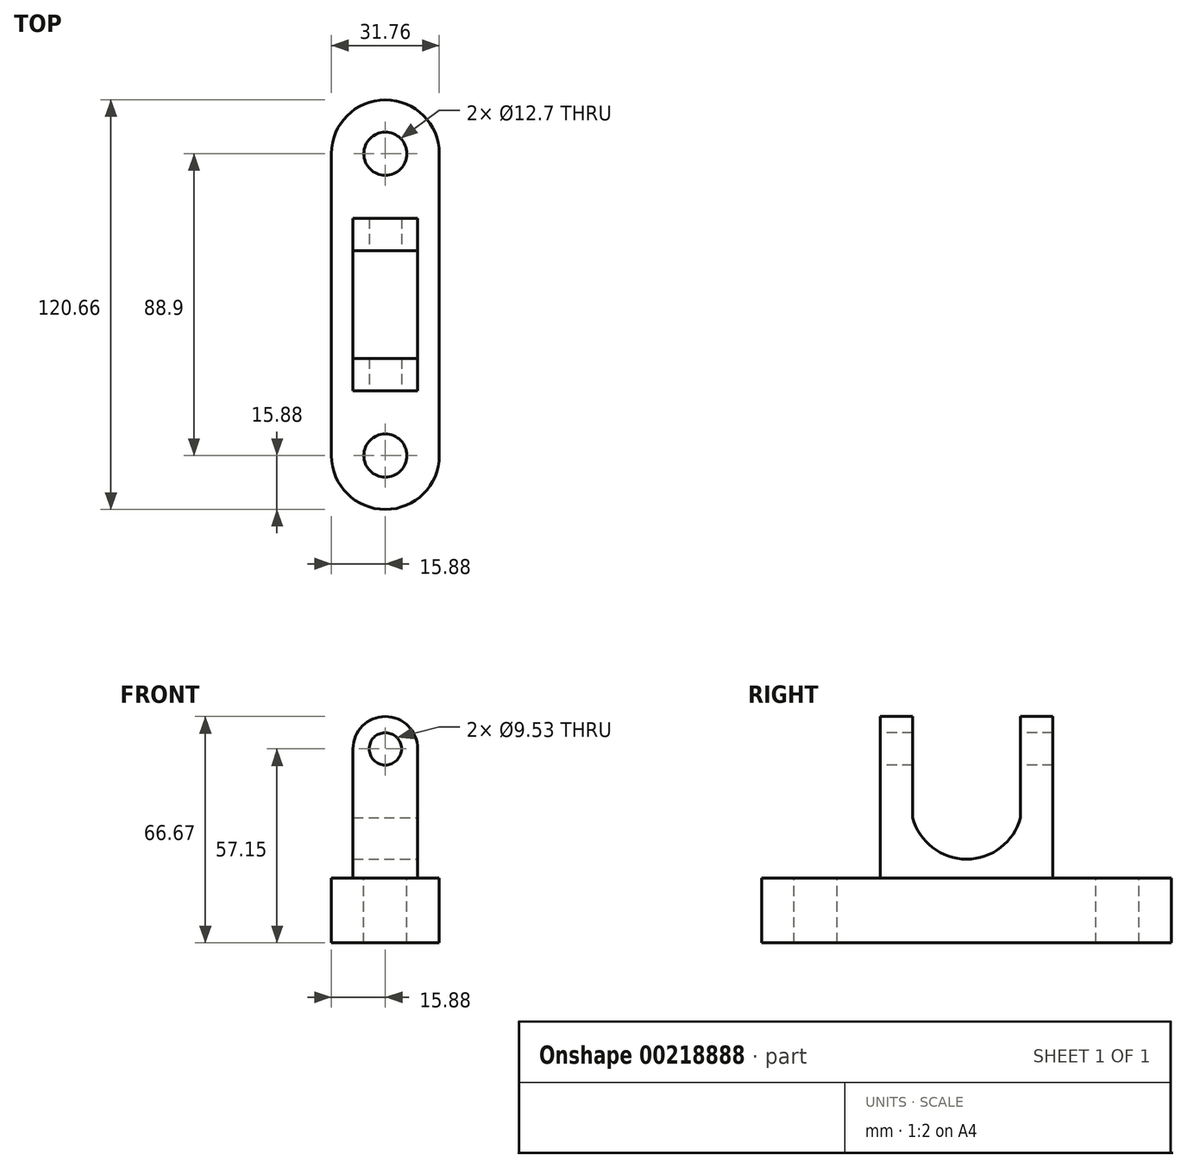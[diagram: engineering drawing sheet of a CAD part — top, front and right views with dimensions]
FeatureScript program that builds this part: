
annotation { "Feature Type Name" : "Feature", "Feature Type Description" : "" }
export const myFeature = defineFeature(function(context is Context, id is Id, definition is map)
    precondition{}
    {
        {
            var Q0;
            Q0=qCreatedBy(makeId("Top.planeOp"),FACE);
            var sketch = newSketch(context, id + "F0", { "sketchPlane" : qUnion([Q0])});
            skLineSegment(sketch, "E0.bottom", {"start": v(15.88, 44.45) * mm, "end": v(-15.88, 44.45) * mm});
            skLineSegment(sketch, "E0.top", {"start": v(15.87, -44.45) * mm, "end": v(-15.87, -44.45) * mm});
            skLineSegment(sketch, "E0.left", {"start": v(15.88, 44.45) * mm, "end": v(15.88, -44.45) * mm});
            skLineSegment(sketch, "E0.right", {"start": v(-15.87, 44.45) * mm, "end": v(-15.88, -44.45) * mm});
            skPoint(sketch, "E0.middle", {"position": v(0, 0) * mm});
            skCircle(sketch, "E1", {"center": v(0, 44.45) * mm, "radius": 15.88 * mm});
            skPoint(sketch, "E1.third.point", {"position": v(0, 60.33) * mm});
            skPoint(sketch, "E1.third.point.positionSnap0", {"position": v(0, 44.45) * mm});
            skCircle(sketch, "E2", {"center": v(0, -44.45) * mm, "radius": 15.88 * mm});
            skPoint(sketch, "E2.third.point", {"position": v(0, -60.32) * mm});
            skPoint(sketch, "E2.third.point.positionSnap0", {"position": v(0, -44.45) * mm});
            skSolve(sketch);
        }
        {
            var Q0;
            Q0 = qSketchRegion(id + "F0", true);
            extrude(context, id + "F1", {"entities" : qUnion([Q0]), "depth" : 19.05 * mm});
        }
        {
            var Q0;
            Q0=makeQuery(id+"F1.opExtrude","CAP_FACE",FACE,{"disambiguationData":[OSD([sQuery(id+"F0.wireOp",EDGE,"E0.left"),sQuery(id+"F0.wireOp",EDGE,"E0.right"),sQuery(id+"F0.wireOp",EDGE,"E1"),sQuery(id+"F0.wireOp",EDGE,"E2")])],"isStart":false});
            var sketch = newSketch(context, id + "F2", { "sketchPlane" : qUnion([Q0])});
            skCircle(sketch, "E3", {"center": v(0, -44.45) * mm, "radius": 6.35 * mm});
            skCircle(sketch, "E4", {"center": v(0, 44.45) * mm, "radius": 6.35 * mm});
            skSolve(sketch);
        }
        {
            var Q0;
            Q0 = qSketchRegion(id + "F2", true);
            extrude(context, id + "F3", {"entities" : qUnion([Q0]), "operationType" : NewBodyOperationType.REMOVE, "oppositeDirection" : true, "depth" : 25.4 * mm});
        }
        {
            var Q0;
            Q0=qCreatedBy(makeId("Front.planeOp"),FACE);
            var sketch = newSketch(context, id + "F4", { "sketchPlane" : qUnion([Q0])});
            skLineSegment(sketch, "E5.0", {"start": v(-15.88, 19.05) * mm, "end": v(15.88, 19.05) * mm});
            skLineSegment(sketch, "E6", {"start": v(-9.53, 19.05) * mm, "end": v(-9.53, 57.15) * mm});
            skLineSegment(sketch, "E7", {"start": v(-9.53, 57.15) * mm, "end": v(9.52, 57.15) * mm});
            skLineSegment(sketch, "E8", {"start": v(9.52, 57.15) * mm, "end": v(9.53, 19.05) * mm});
            skCircle(sketch, "E9", {"center": v(0, 57.15) * mm, "radius": 9.53 * mm});
            skPoint(sketch, "E9.third.point", {"position": v(0, 66.68) * mm});
            skPoint(sketch, "E9.third.point.positionSnap0", {"position": v(0, 57.15) * mm});
            skSolve(sketch);
        }
        {
            var Q0;
            Q0 = qSketchRegion(id + "F4", true);
            extrude(context, id + "F5", {"entities" : qUnion([Q0]), "operationType" : NewBodyOperationType.ADD, "endBound" : BoundingType.SYMMETRIC, "depth" : 50.8 * mm});
        }
        {
            var Q0;
            Q0=makeQuery(id+"F5.opExtrude","CAP_FACE",FACE,{"disambiguationData":[OSD([sQuery(id+"F4.wireOp",EDGE,"E5.0"),sQuery(id+"F4.wireOp",EDGE,"E6"),sQuery(id+"F4.wireOp",EDGE,"E8"),sQuery(id+"F4.wireOp",EDGE,"E9")])],"isStart":false});
            var sketch = newSketch(context, id + "F6", { "sketchPlane" : qUnion([Q0])});
            skCircle(sketch, "E10", {"center": v(0, 57.15) * mm, "radius": 4.76 * mm});
            skSolve(sketch);
        }
        {
            var Q0;
            Q0 = qSketchRegion(id + "F6", true);
            extrude(context, id + "F7", {"entities" : qUnion([Q0]), "operationType" : NewBodyOperationType.REMOVE, "endBound" : BoundingType.UP_TO_NEXT, "oppositeDirection" : true, "depth" : 25.4 * mm});
        }
        {
            var Q0;
            Q0=makeQuery(id+"F5.opExtrude","SWEPT_FACE",FACE,{"disambiguationData":[OSD([sQuery(id+"F4.wireOp",EDGE,"E8")])]});
            var sketch = newSketch(context, id + "F8", { "sketchPlane" : qUnion([Q0])});
            skLineSegment(sketch, "E11", {"start": v(0, 71.85) * mm, "end": v(-15.87, 71.85) * mm});
            skPoint(sketch, "E11.startSnap0", {"position": v(0, 57.15) * mm});
            skLineSegment(sketch, "E12", {"start": v(-15.88, 71.85) * mm, "end": v(-15.87, 36.94) * mm});
            skLineSegment(sketch, "E13", {"start": v(-15.87, 36.94) * mm, "end": v(15.88, 36.94) * mm});
            skLineSegment(sketch, "E14", {"start": v(15.88, 36.94) * mm, "end": v(15.88, 71.85) * mm});
            skLineSegment(sketch, "E15", {"start": v(15.88, 71.85) * mm, "end": v(0, 71.85) * mm});
            skArc(sketch, "E16", {"start": v(-15.87, 36.94) * mm, "mid": v(0, 24.68) * mm, "end": v(15.88, 36.94) * mm});
            skPoint(sketch, "E16.third.point", {"position": v(3.36, 57.15) * mm});
            skArc(sketch, "E17.trimOffspring", {"start": v(15.88, 45.24) * mm, "mid": v(0, 57.5) * mm, "end": v(-15.88, 45.24) * mm});
            skSolve(sketch);
        }
        {
            var Q0;
            Q0 = qSketchRegion(id + "F8", true);
            extrude(context, id + "F9", {"entities" : qUnion([Q0]), "operationType" : NewBodyOperationType.REMOVE, "oppositeDirection" : true, "depth" : 25.4 * mm});
        }
    });
